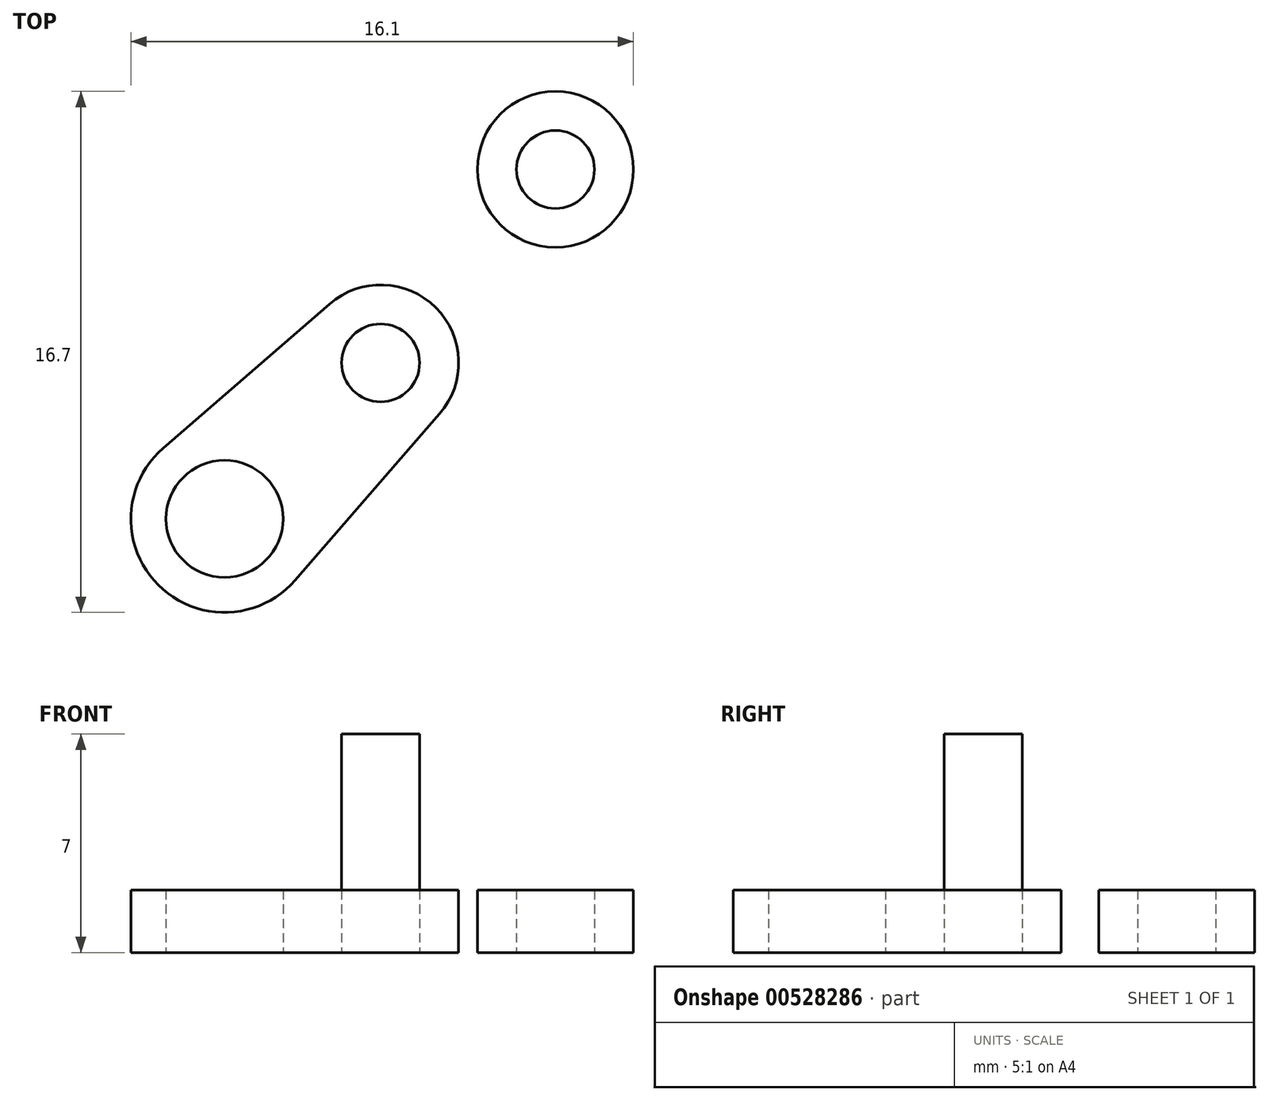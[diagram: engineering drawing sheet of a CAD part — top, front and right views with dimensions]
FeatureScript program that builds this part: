
annotation { "Feature Type Name" : "Feature", "Feature Type Description" : "" }
export const myFeature = defineFeature(function(context is Context, id is Id, definition is map)
    precondition{}
    {
        {
            var Q0;
            Q0=qCreatedBy(makeId("Top.planeOp"),FACE);
            var sketch = newSketch(context, id + "F0", { "sketchPlane" : qUnion([Q0])});
            skLineSegment(sketch, "E0.bottom", {"start": v(0, 0) * mm, "end": v(-36, 0) * mm});
            skLineSegment(sketch, "E0.top", {"start": v(0, 36) * mm, "end": v(-36, 36) * mm});
            skLineSegment(sketch, "E0.left", {"start": v(0, 0) * mm, "end": v(0, 36) * mm});
            skLineSegment(sketch, "E0.right", {"start": v(-36, 0) * mm, "end": v(-36, 36) * mm});
            skCircle(sketch, "E1", {"center": v(-3, 33) * mm, "radius": 1.5 * mm});
            skCircle(sketch, "E2", {"center": v(-3, 3) * mm, "radius": 1.5 * mm});
            skCircle(sketch, "E3", {"center": v(-33, 33) * mm, "radius": 1.5 * mm});
            skCircle(sketch, "E4", {"center": v(-33, 3) * mm, "radius": 1.5 * mm});
            skSolve(sketch);
        }
        {
            var Q0;
            Q0=qCreatedBy(makeId("Top.planeOp"),FACE);
            var sketch = newSketch(context, id + "F1", { "sketchPlane" : qUnion([Q0])});
            skLineSegment(sketch, "E5.bottom", {"start": v(-31.5, 31.5) * mm, "end": v(-4.5, 31.5) * mm});
            skLineSegment(sketch, "E5.top", {"start": v(-31.5, 4.5) * mm, "end": v(-4.5, 4.5) * mm});
            skLineSegment(sketch, "E5.left", {"start": v(-31.5, 31.5) * mm, "end": v(-31.5, 4.5) * mm});
            skLineSegment(sketch, "E5.right", {"start": v(-4.5, 31.5) * mm, "end": v(-4.5, 4.5) * mm});
            skCircle(sketch, "E6", {"center": v(-28, 28) * mm, "radius": 1.5 * mm});
            skCircle(sketch, "E7", {"center": v(-8, 28) * mm, "radius": 1.5 * mm});
            skCircle(sketch, "E8", {"center": v(-8, 8) * mm, "radius": 1.5 * mm});
            skCircle(sketch, "E9", {"center": v(-28, 8) * mm, "radius": 1.5 * mm});
            skSolve(sketch);
        }
        {
            var Q0;
            Q0=qCreatedBy(makeId("Top.planeOp"),FACE);
            var sketch = newSketch(context, id + "F2", { "sketchPlane" : qUnion([Q0])});
            skCircle(sketch, "E10", {"center": v(-28, 8) * mm, "radius": 1.25 * mm});
            skSolve(sketch);
        }
        {
            var Q0;
            Q0=qCreatedBy(makeId("Top.planeOp"),FACE);
            var sketch = newSketch(context, id + "F3", { "sketchPlane" : qUnion([Q0])});
            skCircle(sketch, "E11", {"center": v(-33, 3) * mm, "radius": 1.88 * mm});
            skSolve(sketch);
        }
        {
            var Q0;
            Q0=qCreatedBy(makeId("Top.planeOp"),FACE);
            var sketch = newSketch(context, id + "F4", { "sketchPlane" : qUnion([Q0])});
            skArc(sketch, "E12", {"start": v(-34.97, 5.27) * mm, "mid": v(-35.12, 0.88) * mm, "end": v(-30.73, 1.03) * mm});
            skArc(sketch, "E13", {"start": v(-26.11, 6.36) * mm, "mid": v(-26.23, 9.77) * mm, "end": v(-29.64, 9.89) * mm});
            skLineSegment(sketch, "E14", {"start": v(-34.97, 5.27) * mm, "end": v(-29.64, 9.89) * mm});
            skLineSegment(sketch, "E15", {"start": v(-30.73, 1.03) * mm, "end": v(-26.11, 6.36) * mm});
            skSolve(sketch);
        }
        {
            var Q0;
            Q0 = qSketchRegion(id + "F4", true);
            extrude(context, id + "F5", {"entities" : qUnion([Q0]), "depth" : 2 * mm, "offsetDistance" : 25 * mm});
        }
        {
            var Q0;
            Q0 = qSketchRegion(id + "F3", true);
            extrude(context, id + "F6", {"entities" : qUnion([Q0]), "operationType" : NewBodyOperationType.REMOVE, "depth" : 25 * mm, "offsetDistance" : 25 * mm});
        }
        {
            var Q0;
            Q0 = qSketchRegion(id + "F2", true);
            extrude(context, id + "F7", {"entities" : qUnion([Q0]), "depth" : 7 * mm, "offsetDistance" : 25 * mm});
        }
        {
            var Q0;
            Q0=qCreatedBy(makeId("Top.planeOp"),FACE);
            var sketch = newSketch(context, id + "F8", { "sketchPlane" : qUnion([Q0])});
            skCircle(sketch, "E16", {"center": v(0, 0) * mm, "radius": 1.25 * mm});
            skCircle(sketch, "E17", {"center": v(0, 0) * mm, "radius": 2.5 * mm});
            skSolve(sketch);
        }
        {
            var Q0;
            Q0 = qSketchRegion(id + "F8", true);
            extrude(context, id + "F9", {"entities" : qUnion([Q0]), "depth" : 2 * mm, "offsetDistance" : 25 * mm});
        }
        {
            var Q0;
            Q0=makeQuery(id+"F9.opExtrude","SWEPT_BODY",BODY,{"disambiguationData":[OSD([sQuery(id+"F8.wireOp",EDGE,"E16"),sQuery(id+"F8.wireOp",EDGE,"E17")])]});
            transform(context, id + "F10", {"entities" : qUnion([Q0]), "transformType" : TransformType.TRANSLATION_3D, "dx" : -22.4 * mm, "dy" : 14.2 * mm, "dz" : 0 * mm, "makeCopy" : true});
        }
        {
            var Q0;
            Q0=makeQuery(id+"F9.opExtrude","SWEPT_BODY",BODY,{"disambiguationData":[OSD([sQuery(id+"F8.wireOp",EDGE,"E16"),sQuery(id+"F8.wireOp",EDGE,"E17")])]});
            deleteBodies(context, id + "F11", {"entities" : qUnion([Q0])});
        }
    });
